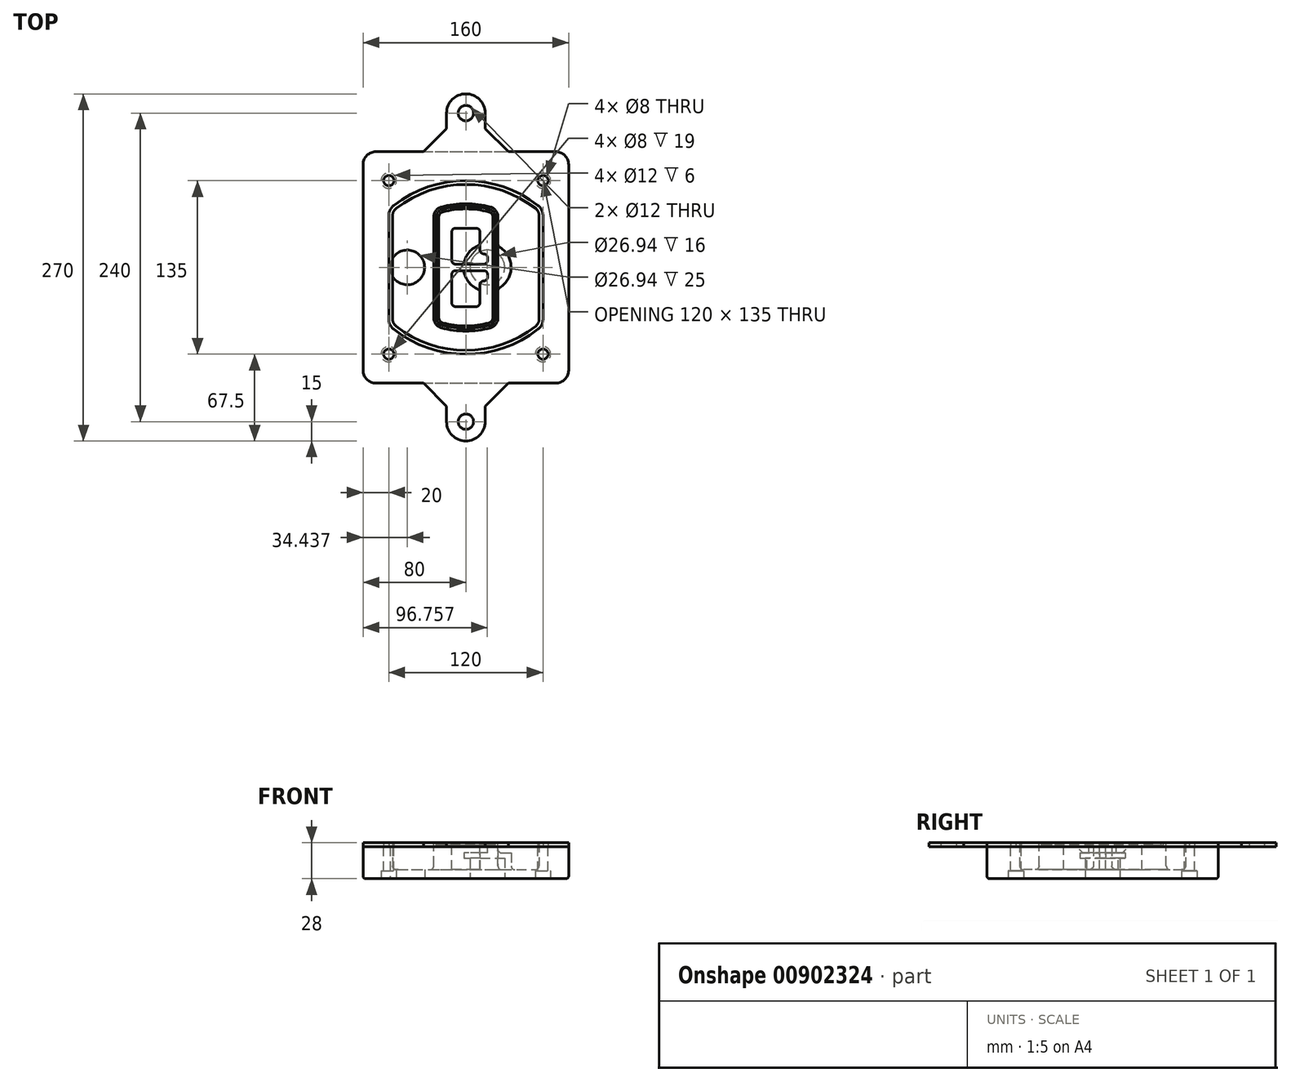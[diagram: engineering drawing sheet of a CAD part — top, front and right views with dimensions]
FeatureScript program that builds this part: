
annotation { "Feature Type Name" : "Feature", "Feature Type Description" : "" }
export const myFeature = defineFeature(function(context is Context, id is Id, definition is map)
    precondition{}
    {
        {
            var Q0;
            Q0=qCreatedBy(makeId("Top.planeOp"),FACE);
            var sketch = newSketch(context, id + "F0", { "sketchPlane" : qUnion([Q0])});
            skPoint(sketch, "E0.rect.middle", {"position": v(0, 0) * mm});
            skLineSegment(sketch, "E1.bottom", {"start": v(-70, -90) * mm, "end": v(70, -90) * mm});
            skLineSegment(sketch, "E1.top", {"start": v(-70, 90) * mm, "end": v(70, 90) * mm});
            skLineSegment(sketch, "E1.left", {"start": v(-80, -80) * mm, "end": v(-80, 80) * mm});
            skLineSegment(sketch, "E1.right", {"start": v(80, -80) * mm, "end": v(80, 80) * mm});
            skLineSegment(sketch, "E2", {"start": v(-80, 90) * mm, "end": v(80, -90) * mm, "construction": true});
            skLineSegment(sketch, "E3", {"start": v(80, 90) * mm, "end": v(-80, -90) * mm, "construction": true});
            skCircle(sketch, "E4", {"center": v(-60, 67.5) * mm, "radius": 4 * mm});
            skCircle(sketch, "E5", {"center": v(60, 67.5) * mm, "radius": 4 * mm});
            skCircle(sketch, "E6", {"center": v(60, -67.5) * mm, "radius": 4 * mm});
            skCircle(sketch, "E7", {"center": v(-60, -67.5) * mm, "radius": 4 * mm});
            skLineSegment(sketch, "E8", {"start": v(-60, 67.5) * mm, "end": v(60, 67.5) * mm, "construction": true});
            skLineSegment(sketch, "E9", {"start": v(60, 67.5) * mm, "end": v(60, -67.5) * mm, "construction": true});
            skLineSegment(sketch, "E10", {"start": v(60, -67.5) * mm, "end": v(-60, -67.5) * mm, "construction": true});
            skLineSegment(sketch, "E11", {"start": v(-60, -67.5) * mm, "end": v(-60, 67.5) * mm, "construction": true});
            skLineSegment(sketch, "E12", {"start": v(-60, 40.3) * mm, "end": v(-60, -40.3) * mm});
            skLineSegment(sketch, "E13", {"start": v(60, 40.3) * mm, "end": v(60, -40.3) * mm});
            skArc(sketch, "E14", {"start": v(56.15, 48.18) * mm, "mid": v(0, 67.5) * mm, "end": v(-56.15, 48.18) * mm});
            skArc(sketch, "E15", {"start": v(-56.15, -48.18) * mm, "mid": v(0, -67.5) * mm, "end": v(56.15, -48.18) * mm});
            skLineSegment(sketch, "E16", {"start": v(-60, 0) * mm, "end": v(60, 0) * mm, "construction": true});
            skPoint(sketch, "E17.visualSharp", {"position": v(-60, -45) * mm});
            skArc(sketch, "E17.filletArc", {"start": v(-60, -40.3) * mm, "mid": v(-58.99, -44.68) * mm, "end": v(-56.15, -48.18) * mm});
            skPoint(sketch, "E18.visualSharp", {"position": v(-60, 45) * mm});
            skArc(sketch, "E18.filletArc", {"start": v(-56.15, 48.18) * mm, "mid": v(-58.99, 44.68) * mm, "end": v(-60, 40.3) * mm});
            skPoint(sketch, "E19.visualSharp", {"position": v(60, 45) * mm});
            skArc(sketch, "E19.filletArc", {"start": v(60, 40.3) * mm, "mid": v(58.99, 44.68) * mm, "end": v(56.15, 48.18) * mm});
            skPoint(sketch, "E20.visualSharp", {"position": v(60, -45) * mm});
            skArc(sketch, "E20.filletArc", {"start": v(56.15, -48.18) * mm, "mid": v(58.99, -44.68) * mm, "end": v(60, -40.3) * mm});
            skPoint(sketch, "E21.visualSharp", {"position": v(-80, 90) * mm});
            skArc(sketch, "E21.filletArc", {"start": v(-70, 90) * mm, "mid": v(-77.07, 87.07) * mm, "end": v(-80, 80) * mm});
            skPoint(sketch, "E22.visualSharp", {"position": v(80, 90) * mm});
            skArc(sketch, "E22.filletArc", {"start": v(80, 80) * mm, "mid": v(77.07, 87.07) * mm, "end": v(70, 90) * mm});
            skPoint(sketch, "E23.visualSharp", {"position": v(80, -90) * mm});
            skArc(sketch, "E23.filletArc", {"start": v(70, -90) * mm, "mid": v(77.07, -87.07) * mm, "end": v(80, -80) * mm});
            skPoint(sketch, "E24.visualSharp", {"position": v(-80, -90) * mm});
            skArc(sketch, "E24.filletArc", {"start": v(-80, -80) * mm, "mid": v(-77.07, -87.07) * mm, "end": v(-70, -90) * mm});
            skArc(sketch, "E25.0", {"start": v(57, 40.3) * mm, "mid": v(56.3, 43.36) * mm, "end": v(54.3, 45.81) * mm});
            skLineSegment(sketch, "E25.1", {"start": v(57, 40.3) * mm, "end": v(57, -40.3) * mm});
            skArc(sketch, "E25.2", {"start": v(54.3, -45.81) * mm, "mid": v(56.3, -43.36) * mm, "end": v(57, -40.3) * mm});
            skArc(sketch, "E25.3", {"start": v(-54.3, -45.81) * mm, "mid": v(0, -64.5) * mm, "end": v(54.3, -45.81) * mm});
            skArc(sketch, "E25.4", {"start": v(-57, -40.3) * mm, "mid": v(-56.3, -43.36) * mm, "end": v(-54.3, -45.81) * mm});
            skArc(sketch, "E25.5", {"start": v(54.3, 45.81) * mm, "mid": v(0, 64.5) * mm, "end": v(-54.3, 45.81) * mm});
            skLineSegment(sketch, "E25.6", {"start": v(-57, 40.3) * mm, "end": v(-57, -40.3) * mm});
            skArc(sketch, "E25.7", {"start": v(-54.3, 45.81) * mm, "mid": v(-56.3, 43.36) * mm, "end": v(-57, 40.3) * mm});
            skArc(sketch, "E26.0", {"start": v(-58.62, 51.33) * mm, "mid": v(-62.58, 46.43) * mm, "end": v(-64, 40.3) * mm});
            skArc(sketch, "E26.1", {"start": v(58.62, 51.33) * mm, "mid": v(0, 71.5) * mm, "end": v(-58.62, 51.33) * mm});
            skArc(sketch, "E26.2", {"start": v(64, 40.3) * mm, "mid": v(62.58, 46.43) * mm, "end": v(58.62, 51.33) * mm});
            skLineSegment(sketch, "E26.3", {"start": v(64, 40.3) * mm, "end": v(64, -40.3) * mm});
            skArc(sketch, "E26.4", {"start": v(58.62, -51.33) * mm, "mid": v(62.58, -46.43) * mm, "end": v(64, -40.3) * mm});
            skLineSegment(sketch, "E26.5", {"start": v(-64, 40.3) * mm, "end": v(-64, -40.3) * mm});
            skArc(sketch, "E26.6", {"start": v(-58.62, -51.33) * mm, "mid": v(0, -71.5) * mm, "end": v(58.62, -51.33) * mm});
            skArc(sketch, "E26.7", {"start": v(-64, -40.3) * mm, "mid": v(-62.58, -46.43) * mm, "end": v(-58.62, -51.33) * mm});
            skSolve(sketch);
        }
        {
            var Q0;
            Q0=makeQuery(id+"F0.imprint","IMPRINT",FACE,{"disambiguationData":[TD([[makeQuery(id+"F0.imprint","IMPRINT",EDGE,{"derivedFrom":sQuery(id+"F0.wireOp",EDGE,"E1.bottom")}),1.0]])]});
            var Q1;
            Q1=makeQuery(id+"F0.imprint","IMPRINT",FACE,{"disambiguationData":[TD([[makeQuery(id+"F0.imprint","IMPRINT",EDGE,{"derivedFrom":sQuery(id+"F0.wireOp",EDGE,"E12")}),1.0]])]});
            var Q2;
            Q2=makeQuery(id+"F0.imprint","IMPRINT",FACE,{"disambiguationData":[TD([[makeQuery(id+"F0.imprint","IMPRINT",EDGE,{"derivedFrom":sQuery(id+"F0.wireOp",EDGE,"E25.0")}),1.0]])]});
            var Q3;
            Q3=makeQuery(id+"F0.imprint","IMPRINT",FACE,{"disambiguationData":[TD([[makeQuery(id+"F0.imprint","IMPRINT",EDGE,{"derivedFrom":sQuery(id+"F0.wireOp",EDGE,"E12")}),-1.0]])]});
            extrude(context, id + "F1", {"entities" : qUnion([Q0, Q1, Q2, Q3]), "oppositeDirection" : true, "depth" : 25 * mm});
        }
        {
            var Q0;
            Q0=makeQuery(id+"F0.imprint","IMPRINT",FACE,{"disambiguationData":[TD([[makeQuery(id+"F0.imprint","IMPRINT",EDGE,{"derivedFrom":sQuery(id+"F0.wireOp",EDGE,"E12")}),1.0]])]});
            extrude(context, id + "F2", {"entities" : qUnion([Q0]), "operationType" : NewBodyOperationType.ADD, "depth" : 3 * mm});
        }
        {
            var Q0;
            Q0=makeQuery(id+"F0.imprint","IMPRINT",FACE,{"disambiguationData":[TD([[makeQuery(id+"F0.imprint","IMPRINT",EDGE,{"derivedFrom":sQuery(id+"F0.wireOp",EDGE,"E25.0")}),1.0]])]});
            extrude(context, id + "F3", {"entities" : qUnion([Q0]), "operationType" : NewBodyOperationType.REMOVE, "oppositeDirection" : true, "depth" : 18 * mm});
        }
        {
            var Q0;
            Q0=makeQuery(id+"F2.opExtrude","CAP_FACE",FACE,{"disambiguationData":[OSD([sQuery(id+"F0.wireOp",EDGE,"E12"),sQuery(id+"F0.wireOp",EDGE,"E13"),sQuery(id+"F0.wireOp",EDGE,"E14"),sQuery(id+"F0.wireOp",EDGE,"E15"),sQuery(id+"F0.wireOp",EDGE,"E17.filletArc"),sQuery(id+"F0.wireOp",EDGE,"E18.filletArc"),sQuery(id+"F0.wireOp",EDGE,"E19.filletArc"),sQuery(id+"F0.wireOp",EDGE,"E20.filletArc"),sQuery(id+"F0.wireOp",EDGE,"E25.0"),sQuery(id+"F0.wireOp",EDGE,"E25.1"),sQuery(id+"F0.wireOp",EDGE,"E25.2"),sQuery(id+"F0.wireOp",EDGE,"E25.3"),sQuery(id+"F0.wireOp",EDGE,"E25.4"),sQuery(id+"F0.wireOp",EDGE,"E25.5"),sQuery(id+"F0.wireOp",EDGE,"E25.6"),sQuery(id+"F0.wireOp",EDGE,"E25.7")])],"isStart":false});
            var sketch = newSketch(context, id + "F4", { "sketchPlane" : qUnion([Q0])});
            skArc(sketch, "E27.0", {"start": v(-19.08, -46.97) * mm, "mid": v(0, -49.5) * mm, "end": v(19.08, -46.97) * mm});
            skArc(sketch, "E28.0", {"start": v(19.08, 46.97) * mm, "mid": v(0, 49.5) * mm, "end": v(-19.08, 46.97) * mm});
            skLineSegment(sketch, "E29", {"start": v(-25, 39.25) * mm, "end": v(-25, -39.25) * mm});
            skLineSegment(sketch, "E30", {"start": v(25, 39.25) * mm, "end": v(25, -39.25) * mm});
            skLineSegment(sketch, "E31", {"start": v(-25, 45.1) * mm, "end": v(25, 45.1) * mm, "construction": true});
            skLineSegment(sketch, "E32", {"start": v(-25, -45.1) * mm, "end": v(25, -45.1) * mm, "construction": true});
            skPoint(sketch, "E33.visualSharp", {"position": v(-25, 45.1) * mm});
            skArc(sketch, "E33.filletArc", {"start": v(-19.08, 46.97) * mm, "mid": v(-23.35, 44.11) * mm, "end": v(-25, 39.25) * mm});
            skPoint(sketch, "E34.visualSharp", {"position": v(25, 45.1) * mm});
            skArc(sketch, "E34.filletArc", {"start": v(25, 39.25) * mm, "mid": v(23.35, 44.11) * mm, "end": v(19.08, 46.97) * mm});
            skPoint(sketch, "E35.visualSharp", {"position": v(25, -45.1) * mm});
            skArc(sketch, "E35.filletArc", {"start": v(19.08, -46.97) * mm, "mid": v(23.35, -44.11) * mm, "end": v(25, -39.25) * mm});
            skPoint(sketch, "E36.visualSharp", {"position": v(-25, -45.1) * mm});
            skArc(sketch, "E36.filletArc", {"start": v(-25, -39.25) * mm, "mid": v(-23.35, -44.11) * mm, "end": v(-19.08, -46.97) * mm});
            skArc(sketch, "E37.0", {"start": v(54.3, 45.81) * mm, "mid": v(0, 64.5) * mm, "end": v(-54.3, 45.81) * mm});
            skArc(sketch, "E37.1", {"start": v(-54.3, 45.81) * mm, "mid": v(-56.3, 43.36) * mm, "end": v(-57, 40.3) * mm});
            skLineSegment(sketch, "E37.2", {"start": v(-57, 40.3) * mm, "end": v(-57, -40.3) * mm});
            skArc(sketch, "E37.3", {"start": v(-57, -40.3) * mm, "mid": v(-56.3, -43.36) * mm, "end": v(-54.3, -45.81) * mm});
            skArc(sketch, "E37.4", {"start": v(-54.3, -45.81) * mm, "mid": v(0, -64.5) * mm, "end": v(54.3, -45.81) * mm});
            skArc(sketch, "E37.5", {"start": v(54.3, -45.81) * mm, "mid": v(56.3, -43.36) * mm, "end": v(57, -40.3) * mm});
            skLineSegment(sketch, "E37.6", {"start": v(57, 40.3) * mm, "end": v(57, -40.3) * mm});
            skArc(sketch, "E37.7", {"start": v(57, 40.3) * mm, "mid": v(56.3, 43.36) * mm, "end": v(54.3, 45.81) * mm});
            skLineSegment(sketch, "E38.0", {"start": v(23, 39.25) * mm, "end": v(23, -39.25) * mm});
            skArc(sketch, "E38.1", {"start": v(18.56, -45.04) * mm, "mid": v(21.76, -42.9) * mm, "end": v(23, -39.25) * mm});
            skArc(sketch, "E38.2", {"start": v(-18.56, -45.04) * mm, "mid": v(0, -47.5) * mm, "end": v(18.56, -45.04) * mm});
            skArc(sketch, "E38.3", {"start": v(-23, -39.25) * mm, "mid": v(-21.76, -42.9) * mm, "end": v(-18.56, -45.04) * mm});
            skLineSegment(sketch, "E38.4", {"start": v(-23, 39.25) * mm, "end": v(-23, -39.25) * mm});
            skArc(sketch, "E38.5", {"start": v(23, 39.25) * mm, "mid": v(21.76, 42.9) * mm, "end": v(18.56, 45.04) * mm});
            skArc(sketch, "E38.6", {"start": v(-18.56, 45.04) * mm, "mid": v(-21.76, 42.9) * mm, "end": v(-23, 39.25) * mm});
            skArc(sketch, "E38.7", {"start": v(18.56, 45.04) * mm, "mid": v(0, 47.5) * mm, "end": v(-18.56, 45.04) * mm});
            skArc(sketch, "E39.0", {"start": v(21, 39.25) * mm, "mid": v(20.18, 41.68) * mm, "end": v(18.04, 43.1) * mm});
            skLineSegment(sketch, "E39.1", {"start": v(21, 39.25) * mm, "end": v(21, -39.25) * mm});
            skArc(sketch, "E39.2", {"start": v(18.04, -43.1) * mm, "mid": v(20.18, -41.68) * mm, "end": v(21, -39.25) * mm});
            skArc(sketch, "E39.3", {"start": v(-18.04, -43.1) * mm, "mid": v(0, -45.5) * mm, "end": v(18.04, -43.1) * mm});
            skArc(sketch, "E39.4", {"start": v(-21, -39.25) * mm, "mid": v(-20.18, -41.68) * mm, "end": v(-18.04, -43.1) * mm});
            skArc(sketch, "E39.5", {"start": v(18.04, 43.1) * mm, "mid": v(0, 45.5) * mm, "end": v(-18.04, 43.1) * mm});
            skLineSegment(sketch, "E39.6", {"start": v(-21, 39.25) * mm, "end": v(-21, -39.25) * mm});
            skArc(sketch, "E39.7", {"start": v(-18.04, 43.1) * mm, "mid": v(-20.18, 41.68) * mm, "end": v(-21, 39.25) * mm});
            skLineSegment(sketch, "E40", {"start": v(-25, 0) * mm, "end": v(25, 0) * mm, "construction": true});
            skLineSegment(sketch, "E41", {"start": v(-11, 5.5) * mm, "end": v(-11, 27.5) * mm});
            skLineSegment(sketch, "E42", {"start": v(-8, 30.5) * mm, "end": v(8, 30.5) * mm});
            skLineSegment(sketch, "E43", {"start": v(11, 27.5) * mm, "end": v(11, 13.5) * mm});
            skLineSegment(sketch, "E44", {"start": v(14, 10.5) * mm, "end": v(14, 10.5) * mm});
            skLineSegment(sketch, "E45", {"start": v(17, 7.5) * mm, "end": v(17, 5.5) * mm});
            skLineSegment(sketch, "E46", {"start": v(14, 2.5) * mm, "end": v(-8, 2.5) * mm});
            skPoint(sketch, "E47.visualSharp", {"position": v(-11, 30.5) * mm});
            skArc(sketch, "E47.filletArc", {"start": v(-8, 30.5) * mm, "mid": v(-10.12, 29.62) * mm, "end": v(-11, 27.5) * mm});
            skPoint(sketch, "E48.visualSharp", {"position": v(11, 30.5) * mm});
            skArc(sketch, "E48.filletArc", {"start": v(11, 27.5) * mm, "mid": v(10.12, 29.62) * mm, "end": v(8, 30.5) * mm});
            skPoint(sketch, "E49.visualSharp", {"position": v(11, 10.5) * mm});
            skArc(sketch, "E49.filletArc", {"start": v(11, 13.5) * mm, "mid": v(11.88, 11.38) * mm, "end": v(14, 10.5) * mm});
            skPoint(sketch, "E50.visualSharp", {"position": v(17, 10.5) * mm});
            skArc(sketch, "E50.filletArc", {"start": v(17, 7.5) * mm, "mid": v(16.12, 9.62) * mm, "end": v(14, 10.5) * mm});
            skPoint(sketch, "E51.visualSharp", {"position": v(17, 2.5) * mm});
            skArc(sketch, "E51.filletArc", {"start": v(14, 2.5) * mm, "mid": v(16.12, 3.38) * mm, "end": v(17, 5.5) * mm});
            skPoint(sketch, "E52.visualSharp", {"position": v(-11, 2.5) * mm});
            skArc(sketch, "E52.filletArc", {"start": v(-11, 5.5) * mm, "mid": v(-10.12, 3.38) * mm, "end": v(-8, 2.5) * mm});
            skLineSegment(sketch, "E53.0.MirrorCS", {"start": v(14, -2.5) * mm, "end": v(-8, -2.5) * mm});
            skArc(sketch, "E54.0.MirrorCS", {"start": v(-11, -5.5) * mm, "mid": v(-10.12, -3.38) * mm, "end": v(-8, -2.5) * mm});
            skLineSegment(sketch, "E55.0.MirrorCS", {"start": v(-11, -5.5) * mm, "end": v(-11, -27.5) * mm});
            skArc(sketch, "E56.0.MirrorCS", {"start": v(-8, -30.5) * mm, "mid": v(-10.12, -29.62) * mm, "end": v(-11, -27.5) * mm});
            skLineSegment(sketch, "E57.0.MirrorCS", {"start": v(-8, -30.5) * mm, "end": v(8, -30.5) * mm});
            skArc(sketch, "E58.0.MirrorCS", {"start": v(11, -27.5) * mm, "mid": v(10.12, -29.62) * mm, "end": v(8, -30.5) * mm});
            skLineSegment(sketch, "E59.0.MirrorCS", {"start": v(11, -27.5) * mm, "end": v(11, -13.5) * mm});
            skArc(sketch, "E60.0.MirrorCS", {"start": v(11, -13.5) * mm, "mid": v(11.88, -11.38) * mm, "end": v(14, -10.5) * mm});
            skArc(sketch, "E61.0.MirrorCS", {"start": v(17, -7.5) * mm, "mid": v(16.12, -9.62) * mm, "end": v(14, -10.5) * mm});
            skLineSegment(sketch, "E62.0.MirrorCS", {"start": v(17, -7.5) * mm, "end": v(17, -5.5) * mm});
            skArc(sketch, "E63.0.MirrorCS", {"start": v(14, -2.5) * mm, "mid": v(16.12, -3.38) * mm, "end": v(17, -5.5) * mm});
            skSolve(sketch);
        }
        {
            var Q0;
            Q0=makeQuery(id+"F4.imprint","IMPRINT",FACE,{"disambiguationData":[TD([[makeQuery(id+"F4.imprint","IMPRINT",EDGE,{"derivedFrom":sQuery(id+"F4.wireOp",EDGE,"E27.0")}),1.0]])]});
            var Q1;
            Q1=makeQuery(id+"F4.imprint","IMPRINT",FACE,{"disambiguationData":[TD([[makeQuery(id+"F4.imprint","IMPRINT",EDGE,{"derivedFrom":sQuery(id+"F4.wireOp",EDGE,"E38.0")}),-1.0]])]});
            var Q2;
            Q2=makeQuery(id+"F4.imprint","IMPRINT",FACE,{"disambiguationData":[TD([[makeQuery(id+"F4.imprint","IMPRINT",EDGE,{"derivedFrom":sQuery(id+"F4.wireOp",EDGE,"E39.0")}),1.0]])]});
            extrude(context, id + "F5", {"entities" : qUnion([Q0, Q1, Q2]), "operationType" : NewBodyOperationType.ADD, "endBound" : BoundingType.UP_TO_NEXT, "oppositeDirection" : true, "depth" : 25 * mm});
        }
        {
            var Q0;
            Q0=makeQuery(id+"F4.imprint","IMPRINT",FACE,{"disambiguationData":[TD([[makeQuery(id+"F4.imprint","IMPRINT",EDGE,{"derivedFrom":sQuery(id+"F4.wireOp",EDGE,"E38.0")}),-1.0]])]});
            extrude(context, id + "F6", {"entities" : qUnion([Q0]), "operationType" : NewBodyOperationType.REMOVE, "oppositeDirection" : true, "depth" : 2 * mm});
        }
        {
            var Q0;
            Q0=makeQuery(id+"F1.opExtrude","CAP_FACE",FACE,{"disambiguationData":[OSD([sQuery(id+"F0.wireOp",EDGE,"E1.bottom"),sQuery(id+"F0.wireOp",EDGE,"E1.top"),sQuery(id+"F0.wireOp",EDGE,"E1.left"),sQuery(id+"F0.wireOp",EDGE,"E1.right"),sQuery(id+"F0.wireOp",EDGE,"E4"),sQuery(id+"F0.wireOp",EDGE,"E5"),sQuery(id+"F0.wireOp",EDGE,"E6"),sQuery(id+"F0.wireOp",EDGE,"E7"),sQuery(id+"F0.wireOp",EDGE,"E21.filletArc"),sQuery(id+"F0.wireOp",EDGE,"E22.filletArc"),sQuery(id+"F0.wireOp",EDGE,"E23.filletArc"),sQuery(id+"F0.wireOp",EDGE,"E24.filletArc")])],"isStart":false});
            var sketch = newSketch(context, id + "F7", { "sketchPlane" : qUnion([Q0])});
            skCircle(sketch, "E64", {"center": v(16.76, 0) * mm, "radius": 13.47 * mm});
            skCircle(sketch, "E65", {"center": v(-45.56, 0) * mm, "radius": 13.47 * mm});
            skLineSegment(sketch, "E66", {"start": v(80, 0) * mm, "end": v(-80, 0) * mm});
            skCircle(sketch, "E67", {"center": v(16.76, 0) * mm, "radius": 18.47 * mm});
            skCircle(sketch, "E68", {"center": v(60, -67.5) * mm, "radius": 6 * mm});
            skCircle(sketch, "E69", {"center": v(-60, -67.5) * mm, "radius": 6 * mm});
            skCircle(sketch, "E70", {"center": v(-60, 67.5) * mm, "radius": 6 * mm});
            skCircle(sketch, "E71", {"center": v(60, 67.5) * mm, "radius": 6 * mm});
            skSolve(sketch);
        }
        {
            var Q0;
            {var subQ1=sQuery(id+"F7.wireOp",EDGE,"E66");var subQ4=sQuery(id+"F7.wireOp",EDGE,"E64");var subQ6=makeQuery(id+"F7.imprint","INTERSECT",VERTEX,{"disambiguationData":[OD(0.0)],"derivedFrom":[subQ4,subQ1]});Q0=makeQuery(id+"F7.imprint","IMPRINT",FACE,{"disambiguationData":[TD([[makeQuery(id+"F7.imprint","IMPRINT",EDGE,{"disambiguationData":[TD([[subQ6,-1.0]])],"derivedFrom":subQ4}),-1.0]])]});}
            var Q1;
            {var subQ0=sQuery(id+"F7.wireOp",EDGE,"E66");var subQ1=sQuery(id+"F7.wireOp",EDGE,"E64");var subQ3=makeQuery(id+"F7.imprint","INTERSECT",VERTEX,{"disambiguationData":[OD(0.0)],"derivedFrom":[subQ1,subQ0]});Q1=makeQuery(id+"F7.imprint","IMPRINT",FACE,{"disambiguationData":[TD([[makeQuery(id+"F7.imprint","IMPRINT",EDGE,{"disambiguationData":[TD([[subQ3,-1.0]])],"derivedFrom":subQ1}),1.0]])]});}
            var Q2;
            {var subQ0=sQuery(id+"F7.wireOp",EDGE,"E66");var subQ1=sQuery(id+"F7.wireOp",EDGE,"E64");var subQ3=makeQuery(id+"F7.imprint","INTERSECT",VERTEX,{"disambiguationData":[OD(0.0)],"derivedFrom":[subQ1,subQ0]});Q2=makeQuery(id+"F7.imprint","IMPRINT",FACE,{"disambiguationData":[TD([[makeQuery(id+"F7.imprint","IMPRINT",EDGE,{"disambiguationData":[TD([[subQ3,1.0]])],"derivedFrom":subQ1}),1.0]])]});}
            var Q3;
            {var subQ1=sQuery(id+"F7.wireOp",EDGE,"E66");var subQ4=sQuery(id+"F7.wireOp",EDGE,"E64");var subQ6=makeQuery(id+"F7.imprint","INTERSECT",VERTEX,{"disambiguationData":[OD(0.0)],"derivedFrom":[subQ4,subQ1]});Q3=makeQuery(id+"F7.imprint","IMPRINT",FACE,{"disambiguationData":[TD([[makeQuery(id+"F7.imprint","IMPRINT",EDGE,{"disambiguationData":[TD([[subQ6,1.0]])],"derivedFrom":subQ4}),-1.0]])]});}
            extrude(context, id + "F8", {"entities" : qUnion([Q0, Q1, Q2, Q3]), "operationType" : NewBodyOperationType.ADD, "oppositeDirection" : true, "depth" : 20 * mm});
        }
        {
            var Q0;
            {var subQ0=sQuery(id+"F7.wireOp",EDGE,"E66");var subQ1=sQuery(id+"F7.wireOp",EDGE,"E64");var subQ3=makeQuery(id+"F7.imprint","INTERSECT",VERTEX,{"disambiguationData":[OD(0.0)],"derivedFrom":[subQ1,subQ0]});Q0=makeQuery(id+"F7.imprint","IMPRINT",FACE,{"disambiguationData":[TD([[makeQuery(id+"F7.imprint","IMPRINT",EDGE,{"disambiguationData":[TD([[subQ3,-1.0]])],"derivedFrom":subQ1}),1.0]])]});}
            var Q1;
            {var subQ0=sQuery(id+"F7.wireOp",EDGE,"E66");var subQ1=sQuery(id+"F7.wireOp",EDGE,"E64");var subQ3=makeQuery(id+"F7.imprint","INTERSECT",VERTEX,{"disambiguationData":[OD(0.0)],"derivedFrom":[subQ1,subQ0]});Q1=makeQuery(id+"F7.imprint","IMPRINT",FACE,{"disambiguationData":[TD([[makeQuery(id+"F7.imprint","IMPRINT",EDGE,{"disambiguationData":[TD([[subQ3,1.0]])],"derivedFrom":subQ1}),1.0]])]});}
            extrude(context, id + "F9", {"entities" : qUnion([Q0, Q1]), "operationType" : NewBodyOperationType.REMOVE, "oppositeDirection" : true, "depth" : 16 * mm});
        }
        {
            var Q0;
            {var subQ0=sQuery(id+"F7.wireOp",EDGE,"E66");var subQ1=sQuery(id+"F7.wireOp",EDGE,"E65");var subQ3=makeQuery(id+"F7.imprint","INTERSECT",VERTEX,{"disambiguationData":[OD(0.0)],"derivedFrom":[subQ1,subQ0]});Q0=makeQuery(id+"F7.imprint","IMPRINT",FACE,{"disambiguationData":[TD([[makeQuery(id+"F7.imprint","IMPRINT",EDGE,{"disambiguationData":[TD([[subQ3,-1.0]])],"derivedFrom":subQ1}),1.0]])]});}
            var Q1;
            {var subQ0=sQuery(id+"F7.wireOp",EDGE,"E66");var subQ1=sQuery(id+"F7.wireOp",EDGE,"E65");var subQ3=makeQuery(id+"F7.imprint","INTERSECT",VERTEX,{"disambiguationData":[OD(0.0)],"derivedFrom":[subQ1,subQ0]});Q1=makeQuery(id+"F7.imprint","IMPRINT",FACE,{"disambiguationData":[TD([[makeQuery(id+"F7.imprint","IMPRINT",EDGE,{"disambiguationData":[TD([[subQ3,1.0]])],"derivedFrom":subQ1}),1.0]])]});}
            extrude(context, id + "F10", {"entities" : qUnion([Q0, Q1]), "operationType" : NewBodyOperationType.REMOVE, "oppositeDirection" : true, "depth" : 25 * mm});
        }
        {
            var Q0;
            Q0=makeQuery(id+"F7.imprint","IMPRINT",FACE,{"disambiguationData":[TD([[makeQuery(id+"F7.imprint","IMPRINT",EDGE,{"derivedFrom":sQuery(id+"F7.wireOp",EDGE,"E68")}),1.0]])]});
            var Q1;
            Q1=makeQuery(id+"F7.imprint","IMPRINT",FACE,{"disambiguationData":[TD([[makeQuery(id+"F7.imprint","IMPRINT",EDGE,{"derivedFrom":makeQuery(id+"F1.opExtrude","CAP_EDGE",EDGE,{"disambiguationData":[OSD([sQuery(id+"F0.wireOp",EDGE,"E5")])],"isStart":false})}),-1.0]])]});
            var Q2;
            Q2=makeQuery(id+"F7.imprint","IMPRINT",FACE,{"disambiguationData":[TD([[makeQuery(id+"F7.imprint","IMPRINT",EDGE,{"derivedFrom":sQuery(id+"F7.wireOp",EDGE,"E69")}),1.0]])]});
            var Q3;
            Q3=makeQuery(id+"F7.imprint","IMPRINT",FACE,{"disambiguationData":[TD([[makeQuery(id+"F7.imprint","IMPRINT",EDGE,{"derivedFrom":makeQuery(id+"F1.opExtrude","CAP_EDGE",EDGE,{"disambiguationData":[OSD([sQuery(id+"F0.wireOp",EDGE,"E4")])],"isStart":false})}),-1.0]])]});
            var Q4;
            Q4=makeQuery(id+"F7.imprint","IMPRINT",FACE,{"disambiguationData":[TD([[makeQuery(id+"F7.imprint","IMPRINT",EDGE,{"derivedFrom":sQuery(id+"F7.wireOp",EDGE,"E70")}),1.0]])]});
            var Q5;
            Q5=makeQuery(id+"F7.imprint","IMPRINT",FACE,{"disambiguationData":[TD([[makeQuery(id+"F7.imprint","IMPRINT",EDGE,{"derivedFrom":makeQuery(id+"F1.opExtrude","CAP_EDGE",EDGE,{"disambiguationData":[OSD([sQuery(id+"F0.wireOp",EDGE,"E7")])],"isStart":false})}),-1.0]])]});
            var Q6;
            Q6=makeQuery(id+"F7.imprint","IMPRINT",FACE,{"disambiguationData":[TD([[makeQuery(id+"F7.imprint","IMPRINT",EDGE,{"derivedFrom":sQuery(id+"F7.wireOp",EDGE,"E71")}),1.0]])]});
            var Q7;
            Q7=makeQuery(id+"F7.imprint","IMPRINT",FACE,{"disambiguationData":[TD([[makeQuery(id+"F7.imprint","IMPRINT",EDGE,{"derivedFrom":makeQuery(id+"F1.opExtrude","CAP_EDGE",EDGE,{"disambiguationData":[OSD([sQuery(id+"F0.wireOp",EDGE,"E6")])],"isStart":false})}),-1.0]])]});
            extrude(context, id + "F11", {"entities" : qUnion([Q0, Q1, Q2, Q3, Q4, Q5, Q6, Q7]), "operationType" : NewBodyOperationType.REMOVE, "oppositeDirection" : true, "depth" : 6 * mm});
        }
        {
            var Q0;
            Q0=makeQuery(id+"F9.boolean.opBoolean","COPY",FACE,{"derivedFrom":makeQuery(id+"F9.opExtrude","CAP_FACE",FACE,{"disambiguationData":[OSD([sQuery(id+"F7.wireOp",EDGE,"E64")])],"isStart":false})});
            var sketch = newSketch(context, id + "F12", { "sketchPlane" : qUnion([Q0])});
            skArc(sketch, "E72.0", {"start": v(11, 17.55) * mm, "mid": v(2.57, 11.82) * mm, "end": v(-1.54, 2.5) * mm});
            skArc(sketch, "E72.1", {"start": v(-1.54, -2.5) * mm, "mid": v(2.57, -11.82) * mm, "end": v(11, -17.55) * mm});
            skLineSegment(sketch, "E73", {"start": v(-1.54, -2.5) * mm, "end": v(14, -2.5) * mm});
            skLineSegment(sketch, "E74.0", {"start": v(14, 2.5) * mm, "end": v(-1.54, 2.5) * mm});
            skArc(sketch, "E74.1", {"start": v(14, 2.5) * mm, "mid": v(16.12, 3.38) * mm, "end": v(17, 5.5) * mm});
            skLineSegment(sketch, "E74.2", {"start": v(17, 7.5) * mm, "end": v(17, 5.5) * mm});
            skArc(sketch, "E74.3", {"start": v(17, 7.5) * mm, "mid": v(16.12, 9.62) * mm, "end": v(14, 10.5) * mm});
            skArc(sketch, "E74.4", {"start": v(11, 13.5) * mm, "mid": v(11.88, 11.38) * mm, "end": v(14, 10.5) * mm});
            skLineSegment(sketch, "E74.5", {"start": v(11, 17.55) * mm, "end": v(11, 13.5) * mm});
            skLineSegment(sketch, "E74.7", {"start": v(14, -2.5) * mm, "end": v(-1.54, -2.5) * mm});
            skArc(sketch, "E74.8", {"start": v(14, -2.5) * mm, "mid": v(16.12, -3.38) * mm, "end": v(17, -5.5) * mm});
            skLineSegment(sketch, "E74.9", {"start": v(17, -7.5) * mm, "end": v(17, -5.5) * mm});
            skArc(sketch, "E74.10", {"start": v(17, -7.5) * mm, "mid": v(16.12, -9.62) * mm, "end": v(14, -10.5) * mm});
            skArc(sketch, "E74.11", {"start": v(11, -13.5) * mm, "mid": v(11.88, -11.38) * mm, "end": v(14, -10.5) * mm});
            skLineSegment(sketch, "E74.12", {"start": v(11, -17.55) * mm, "end": v(11, -13.5) * mm});
            skPoint(sketch, "E75.orphan", {"position": v(11, -27.5) * mm});
            skPoint(sketch, "E76.orphan", {"position": v(-8, -2.5) * mm});
            skPoint(sketch, "E77.orphan", {"position": v(-8, 2.5) * mm});
            skPoint(sketch, "E78.orphan", {"position": v(11, 27.5) * mm});
            skSolve(sketch);
        }
        {
            var Q0;
            {var subQ7=sQuery(id+"F12.wireOp",EDGE,"E72.0");var subQ14=sQuery(id+"F12.wireOp",EDGE,"E72.1");var subQ16=sQuery(id+"F12.wireOp",EDGE,"E74.1");var subQ18=sQuery(id+"F12.wireOp",EDGE,"E74.8");Q0=qUnion([makeQuery(id+"F12.imprint","IMPRINT",FACE,{"disambiguationData":[TD([[makeQuery(id+"F12.imprint","IMPRINT",EDGE,{"derivedFrom":subQ7}),1.0]])]}),makeQuery(id+"F12.imprint","IMPRINT",FACE,{"disambiguationData":[TD([[makeQuery(id+"F12.imprint","IMPRINT",EDGE,{"derivedFrom":subQ14}),1.0]])]}),makeQuery(id+"F12.imprint","IMPRINT",FACE,{"disambiguationData":[TD([[makeQuery(id+"F12.imprint","IMPRINT",EDGE,{"derivedFrom":subQ16}),1.0]])]}),makeQuery(id+"F12.imprint","IMPRINT",FACE,{"disambiguationData":[TD([[makeQuery(id+"F12.imprint","IMPRINT",EDGE,{"derivedFrom":subQ18}),-1.0]])]})]);}
            var Q1;
            Q1=makeQuery(id+"F5.boolean.opBoolean","SPLIT",FACE,{"disambiguationData":[TD([makeQuery(id+"F5.opExtrude","SWEPT_FACE",FACE,{"disambiguationData":[OSD([sQuery(id+"F4.wireOp",EDGE,"E41")])]})])],"derivedFrom":makeQuery(id+"F3.boolean.opBoolean","COPY",FACE,{"derivedFrom":makeQuery(id+"F3.opExtrude","CAP_FACE",FACE,{"disambiguationData":[OSD([sQuery(id+"F0.wireOp",EDGE,"E25.0"),sQuery(id+"F0.wireOp",EDGE,"E25.1"),sQuery(id+"F0.wireOp",EDGE,"E25.2"),sQuery(id+"F0.wireOp",EDGE,"E25.3"),sQuery(id+"F0.wireOp",EDGE,"E25.4"),sQuery(id+"F0.wireOp",EDGE,"E25.5"),sQuery(id+"F0.wireOp",EDGE,"E25.6"),sQuery(id+"F0.wireOp",EDGE,"E25.7")])],"isStart":false})})});
            extrude(context, id + "F13", {"entities" : qUnion([Q0]), "operationType" : NewBodyOperationType.REMOVE, "endBound" : BoundingType.UP_TO_SURFACE, "endBoundEntityFace" : qUnion([Q1]), "depth" : 25 * mm});
        }
        {
            var Q0;
            Q0=makeQuery(id+"F3.boolean.opBoolean","COPY",EDGE,{"derivedFrom":makeQuery(id+"F3.opExtrude","CAP_EDGE",EDGE,{"disambiguationData":[OSD([sQuery(id+"F0.wireOp",EDGE,"E25.6")])],"isStart":false})});
            var Q1;
            Q1=makeQuery(id+"F8.boolean.opBoolean","INTERSECT",EDGE,{"derivedFrom":[makeQuery(id+"F5.opExtrude","SWEPT_FACE",FACE,{"disambiguationData":[OSD([sQuery(id+"F4.wireOp",EDGE,"E30")])]}),makeQuery(id+"F8.opExtrude","CAP_FACE",FACE,{"disambiguationData":[OSD([sQuery(id+"F7.wireOp",EDGE,"E67")])],"isStart":false})]});
            var Q2;
            Q2=makeQuery(id+"F8.boolean.opBoolean","INTERSECT",EDGE,{"disambiguationData":[OD(1.0)],"derivedFrom":[makeQuery(id+"F5.opExtrude","SWEPT_FACE",FACE,{"disambiguationData":[OSD([sQuery(id+"F4.wireOp",EDGE,"E30")])]}),makeQuery(id+"F8.opExtrude","SWEPT_FACE",FACE,{"disambiguationData":[OSD([sQuery(id+"F7.wireOp",EDGE,"E67")])]})]});
            var Q3;
            {var subQ0=sQuery(id+"F4.wireOp",EDGE,"E30");Q3=makeQuery(id+"F8.boolean.opBoolean","SPLIT",EDGE,{"disambiguationData":[TD([makeQuery(id+"F5.opExtrude","SWEPT_FACE",FACE,{"disambiguationData":[OSD([sQuery(id+"F4.wireOp",EDGE,"E35.filletArc")])]})])],"derivedFrom":makeQuery(id+"F5.opExtrude","CAP_EDGE",EDGE,{"disambiguationData":[OSD([subQ0])],"isStart":false})});}
            var Q4;
            {var subQ0=sQuery(id+"F0.wireOp",EDGE,"E25.7");var subQ1=sQuery(id+"F0.wireOp",EDGE,"E25.1");var subQ2=sQuery(id+"F0.wireOp",EDGE,"E25.6");var subQ3=sQuery(id+"F0.wireOp",EDGE,"E25.5");var subQ4=sQuery(id+"F0.wireOp",EDGE,"E25.4");var subQ5=sQuery(id+"F0.wireOp",EDGE,"E25.0");var subQ6=sQuery(id+"F0.wireOp",EDGE,"E25.2");var subQ7=sQuery(id+"F0.wireOp",EDGE,"E25.3");Q4=makeQuery(id+"F8.boolean.opBoolean","INTERSECT",EDGE,{"derivedFrom":[makeQuery(id+"F5.boolean.opBoolean","SPLIT",FACE,{"disambiguationData":[TD([makeQuery(id+"F2.opExtrude","SWEPT_FACE",FACE,{"disambiguationData":[OSD([subQ5])]})])],"derivedFrom":makeQuery(id+"F3.boolean.opBoolean","COPY",FACE,{"derivedFrom":makeQuery(id+"F3.opExtrude","CAP_FACE",FACE,{"disambiguationData":[OSD([subQ5,subQ1,subQ6,subQ7,subQ4,subQ3,subQ2,subQ0])],"isStart":false})})}),makeQuery(id+"F8.opExtrude","SWEPT_FACE",FACE,{"disambiguationData":[OSD([sQuery(id+"F7.wireOp",EDGE,"E67")])]})]});}
            var Q5;
            Q5=makeQuery(id+"F8.boolean.opBoolean","INTERSECT",EDGE,{"disambiguationData":[OD(0.0)],"derivedFrom":[makeQuery(id+"F5.opExtrude","SWEPT_FACE",FACE,{"disambiguationData":[OSD([sQuery(id+"F4.wireOp",EDGE,"E30")])]}),makeQuery(id+"F8.opExtrude","SWEPT_FACE",FACE,{"disambiguationData":[OSD([sQuery(id+"F7.wireOp",EDGE,"E67")])]})]});
            fillet(context, id + "F14", {"entities" : qUnion([Q0, Q1, Q2, Q3, Q4, Q5]), "radius" : 3 * mm, "tangentPropagation" : true, "allowEdgeOverflow" : false});
        }
        {
            var Q0;
            Q0=makeQuery(id+"F1.opExtrude","CAP_EDGE",EDGE,{"disambiguationData":[OSD([sQuery(id+"F0.wireOp",EDGE,"E1.bottom")])],"isStart":false});
            fillet(context, id + "F15", {"entities" : qUnion([Q0]), "radius" : 2 * mm, "tangentPropagation" : true, "allowEdgeOverflow" : false});
        }
        {
            var Q0;
            Q0=qCreatedBy(makeId("Top.planeOp"),FACE);
            var sketch = newSketch(context, id + "F16", { "sketchPlane" : qUnion([Q0])});
            skCircle(sketch, "E79.0", {"center": v(-60, -67.5) * mm, "radius": 4 * mm});
            skArc(sketch, "E79.1", {"start": v(-80, -80) * mm, "mid": v(-77.07, -87.07) * mm, "end": v(-70, -90) * mm});
            skLineSegment(sketch, "E79.2", {"start": v(-70, -90) * mm, "end": v(70, -90) * mm});
            skArc(sketch, "E79.3", {"start": v(70, -90) * mm, "mid": v(77.07, -87.07) * mm, "end": v(80, -80) * mm});
            skLineSegment(sketch, "E79.4", {"start": v(80, -80) * mm, "end": v(80, 80) * mm});
            skArc(sketch, "E79.5", {"start": v(80, 80) * mm, "mid": v(77.07, 87.07) * mm, "end": v(70, 90) * mm});
            skLineSegment(sketch, "E79.6", {"start": v(-70, 90) * mm, "end": v(70, 90) * mm});
            skArc(sketch, "E79.7", {"start": v(-70, 90) * mm, "mid": v(-77.07, 87.07) * mm, "end": v(-80, 80) * mm});
            skLineSegment(sketch, "E79.8", {"start": v(-80, -80) * mm, "end": v(-80, 80) * mm});
            skCircle(sketch, "E79.9", {"center": v(-60, 67.5) * mm, "radius": 4 * mm});
            skCircle(sketch, "E79.10", {"center": v(60, 67.5) * mm, "radius": 4 * mm});
            skCircle(sketch, "E79.11", {"center": v(60, -67.5) * mm, "radius": 4 * mm});
            skArc(sketch, "E79.12", {"start": v(60, 40.3) * mm, "mid": v(58.99, 44.68) * mm, "end": v(56.15, 48.18) * mm});
            skArc(sketch, "E79.13", {"start": v(56.15, 48.18) * mm, "mid": v(0, 67.5) * mm, "end": v(-56.15, 48.18) * mm});
            skArc(sketch, "E79.14", {"start": v(-56.15, 48.18) * mm, "mid": v(-58.99, 44.68) * mm, "end": v(-60, 40.3) * mm});
            skLineSegment(sketch, "E79.15", {"start": v(-60, 40.3) * mm, "end": v(-60, -40.3) * mm});
            skArc(sketch, "E79.16", {"start": v(-60, -40.3) * mm, "mid": v(-58.99, -44.68) * mm, "end": v(-56.15, -48.18) * mm});
            skArc(sketch, "E79.17", {"start": v(-56.15, -48.18) * mm, "mid": v(0, -67.5) * mm, "end": v(56.15, -48.18) * mm});
            skArc(sketch, "E79.18", {"start": v(56.15, -48.18) * mm, "mid": v(58.99, -44.68) * mm, "end": v(60, -40.3) * mm});
            skLineSegment(sketch, "E79.19", {"start": v(60, 40.3) * mm, "end": v(60, -40.3) * mm});
            skLineSegment(sketch, "E80", {"start": v(0, 90) * mm, "end": v(0, 120) * mm, "construction": true});
            skCircle(sketch, "E81", {"center": v(0, 120) * mm, "radius": 6 * mm});
            skArc(sketch, "E82", {"start": v(-15, 120) * mm, "mid": v(0, 135) * mm, "end": v(15, 120) * mm});
            skLineSegment(sketch, "E83", {"start": v(-15, 120) * mm, "end": v(-15, 108) * mm});
            skLineSegment(sketch, "E84", {"start": v(-15, 108) * mm, "end": v(-33, 90) * mm});
            skLineSegment(sketch, "E85", {"start": v(15, 120) * mm, "end": v(15, 108) * mm});
            skLineSegment(sketch, "E86", {"start": v(15, 108) * mm, "end": v(33, 90) * mm});
            skLineSegment(sketch, "E87", {"start": v(-80, 0) * mm, "end": v(80, 0) * mm, "construction": true});
            skLineSegment(sketch, "E88.MirrorCS", {"start": v(-15, -108) * mm, "end": v(-33, -90) * mm});
            skLineSegment(sketch, "E89.MirrorCS", {"start": v(-15, -120) * mm, "end": v(-15, -108) * mm});
            skArc(sketch, "E90.MirrorCS", {"start": v(-15, -120) * mm, "mid": v(0, -135) * mm, "end": v(15, -120) * mm});
            skCircle(sketch, "E91.MirrorC", {"center": v(0, -120) * mm, "radius": 6 * mm});
            skLineSegment(sketch, "E92.MirrorCS", {"start": v(15, -120) * mm, "end": v(15, -108) * mm});
            skLineSegment(sketch, "E93.MirrorCS", {"start": v(15, -108) * mm, "end": v(33, -90) * mm});
            skLineSegment(sketch, "E94.MirrorCS", {"start": v(0, -90) * mm, "end": v(0, -120) * mm, "construction": true});
            skSolve(sketch);
        }
        {
            var Q0;
            Q0 = qSketchRegion(id + "F16", true);
            var Q1;
            Q1=makeQuery(id+"F2.opExtrude","CAP_FACE",FACE,{"disambiguationData":[OSD([sQuery(id+"F0.wireOp",EDGE,"E12"),sQuery(id+"F0.wireOp",EDGE,"E13"),sQuery(id+"F0.wireOp",EDGE,"E14"),sQuery(id+"F0.wireOp",EDGE,"E15"),sQuery(id+"F0.wireOp",EDGE,"E17.filletArc"),sQuery(id+"F0.wireOp",EDGE,"E18.filletArc"),sQuery(id+"F0.wireOp",EDGE,"E19.filletArc"),sQuery(id+"F0.wireOp",EDGE,"E20.filletArc"),sQuery(id+"F0.wireOp",EDGE,"E25.0"),sQuery(id+"F0.wireOp",EDGE,"E25.1"),sQuery(id+"F0.wireOp",EDGE,"E25.2"),sQuery(id+"F0.wireOp",EDGE,"E25.3"),sQuery(id+"F0.wireOp",EDGE,"E25.4"),sQuery(id+"F0.wireOp",EDGE,"E25.5"),sQuery(id+"F0.wireOp",EDGE,"E25.6"),sQuery(id+"F0.wireOp",EDGE,"E25.7")])],"isStart":false});
            extrude(context, id + "F17", {"entities" : qUnion([Q0]), "endBound" : BoundingType.UP_TO_SURFACE, "depth" : 25 * mm, "endBoundEntityFace" : qUnion([Q1]), "offsetDistance" : 25 * mm});
        }
    });
